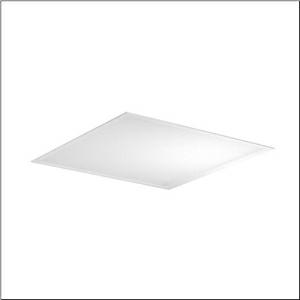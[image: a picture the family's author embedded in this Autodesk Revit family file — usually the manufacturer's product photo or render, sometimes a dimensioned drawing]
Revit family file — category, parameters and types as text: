
# Revit family: apollon_r__21_square_51mq12w72313_b113
name_source: partatom
category: Lighting Fixtures
units: mm (PartAtom-declared; Revit-internal decimal feet)

## family parameters
Cut with Voids When Loaded = No
Host = Face
Light Source = No
Part Type = Normal
Room Calculation Point = No
Round Connector Dimension = Use Diameter
Shared = No

## types (1)
- Apollon® 21 square (1 x LED, 4000 lm, 33 W, 3000K)
    Apparent Load = 33 VA
    CIE Flux Codes = 61 87 97 100 100
    Color Rendering = 80
    Color Temperature = 3000K
    Default Elevation = 1800 mm
    Description = Apollon® 21 square, office luminaire, primary optical cover: micro prismatic cover, of PMMA, CAT 2 (L<= 3000cd/m²), light emission: direct distribution, primary light characteristic: symmetric, installation type: lay-in mounting, LED, rated luminous flux: 4.000lm, luminous efficacy: 121lm/W, light colour: 830, colour temperature: 3000K, control gear: ECG, with terminal, 3-pole, mains connection: 220..240V, AC, 50/60Hz, rated input power: 33W, housing, of aluminium, traffic white (RAL 9016), module: M600, length: 596mm, width: 596mm, height: 40mm, housing upper side, of sheet steel, galvanised, protection rating (complete): IP20, protection rating (lamp compartment, on room side): IP50, insulation class (complete): insulation class II (safety insulation), certification: CE, ENEC, permissible operating ambient temperature: -20..+40°C, packaging unit: 1 piece
    Height = 0 mm  [stored 0 ft]
    Lamp = 1 x LED
    Lamp Light Flux = 4000 lm
    Lamp Power = 33 W
    Lamp count = 1
    Length = 595 mm
    Luminous efficacy = 121 lm/W
    Manufacturer = Siteco
    ModVariant = No
    Model = 51MQ12W72313
    Mounting Place = Ceiling
    Mounting Type = Recessed
    Number of Poles = 1
    OnlyDefault = Yes
    Power Factor = 1
    Product Name = Apollon® 21 square
    Product group = office luminaire | ceiling recessed
    ProductGroupID = 400
    Protection Class = Protection class II
    Protection Degree = IP 20
    RLX_Detail_Level = 1
    RlxData = <blob elided: 14485 chars, md5=5b737f1e>
    Socket = socket
    Standby Power = 0 W
    System Light Flux = 4000 lm
    System Power = 33 W
    Type Comments = Product without accessories
    Type Image = l_1006118.jpg
    URL = http://relux.com
    VarID = ---
    Voltage = 0 V
    Weight = 0.00 kg
    Width = 595 mm

note: [stored X ft] marks values corroborated as IEEE doubles in the binary element streams (Revit-internal decimal feet)

## geometry (parser evidence)
native form markers: Sweep x12
no freeform markers — native parametric forms only
